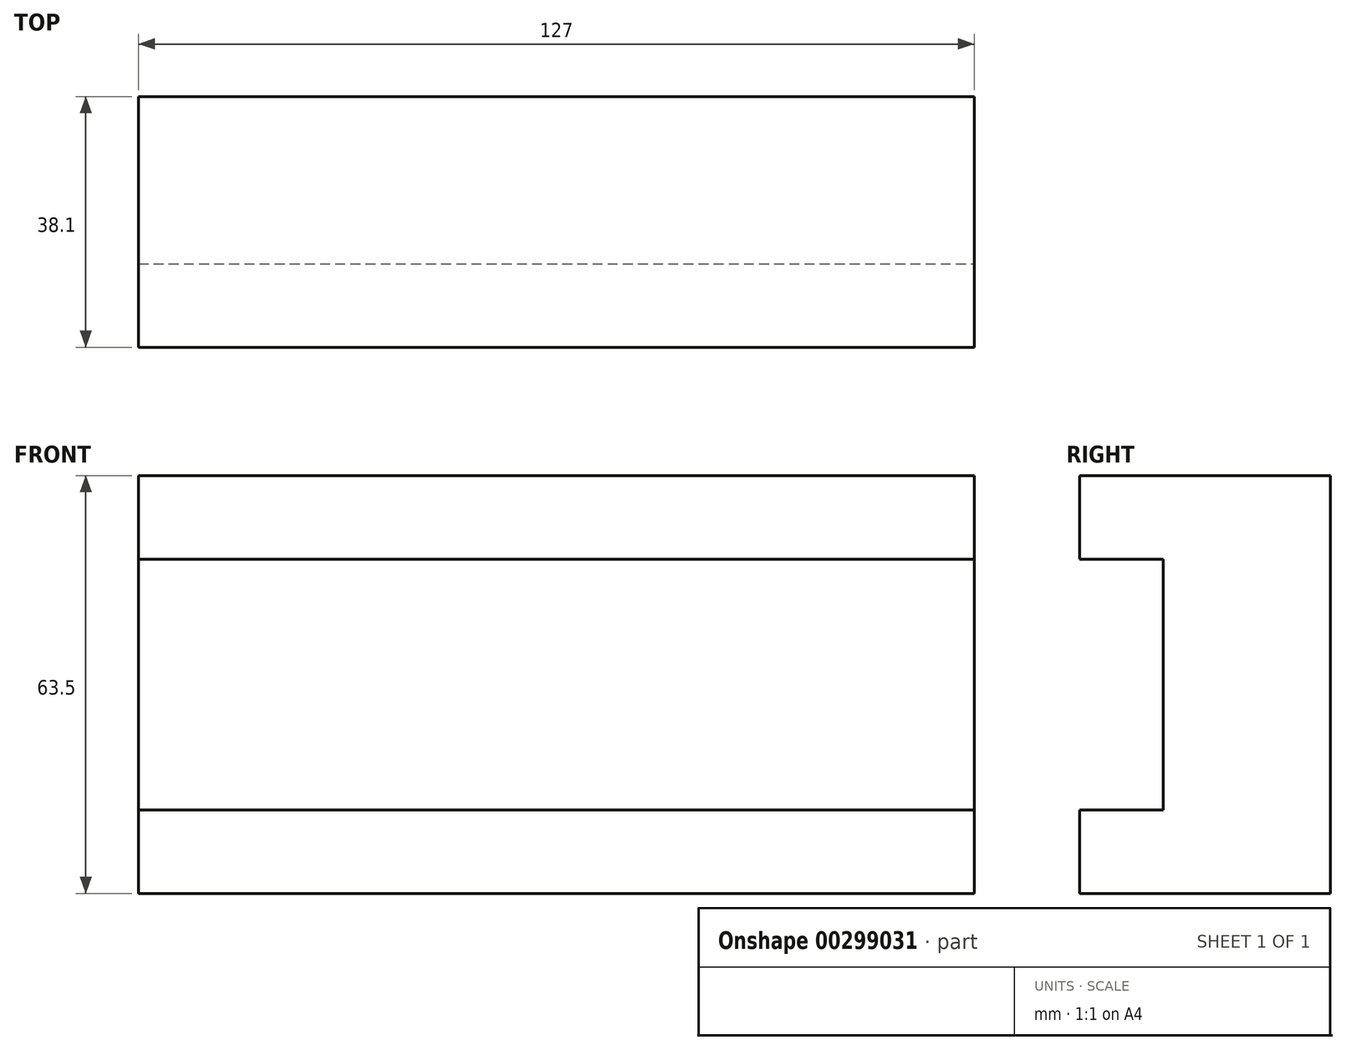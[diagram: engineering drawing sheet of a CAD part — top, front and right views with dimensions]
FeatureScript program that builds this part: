
annotation { "Feature Type Name" : "Feature", "Feature Type Description" : "" }
export const myFeature = defineFeature(function(context is Context, id is Id, definition is map)
    precondition{}
    {
        {
            var Q0;
            Q0=qCreatedBy(makeId("Front.planeOp"),FACE);
            var sketch = newSketch(context, id + "F0", { "sketchPlane" : qUnion([Q0])});
            skLineSegment(sketch, "E0.bottom", {"start": v(-63.5, 31.75) * mm, "end": v(63.5, 31.75) * mm});
            skLineSegment(sketch, "E0.top", {"start": v(-63.5, -31.75) * mm, "end": v(63.5, -31.75) * mm});
            skLineSegment(sketch, "E0.left", {"start": v(-63.5, 31.75) * mm, "end": v(-63.5, -31.75) * mm});
            skLineSegment(sketch, "E0.right", {"start": v(63.5, 31.75) * mm, "end": v(63.5, -31.75) * mm});
            skPoint(sketch, "E0.middle", {"position": v(0, 0) * mm});
            skSolve(sketch);
        }
        {
            var Q0;
            Q0=makeQuery(id+"F0.imprint","IMPRINT",FACE,{"disambiguationData":[TD([[makeQuery(id+"F0.imprint","IMPRINT",EDGE,{"derivedFrom":sQuery(id+"F0.wireOp",EDGE,"E0.bottom")}),-1.0]])]});
            extrude(context, id + "F1", {"entities" : qUnion([Q0]), "depth" : 38.1 * mm});
        }
        {
            var Q0;
            Q0=makeQuery(id+"F1.opExtrude","SWEPT_FACE",FACE,{"disambiguationData":[OSD([sQuery(id+"F0.wireOp",EDGE,"E0.right")])]});
            var sketch = newSketch(context, id + "F2", { "sketchPlane" : qUnion([Q0])});
            skLineSegment(sketch, "E1.bottom", {"start": v(-38.1, 19.05) * mm, "end": v(-25.4, 19.05) * mm});
            skLineSegment(sketch, "E1.top", {"start": v(-38.1, -19.05) * mm, "end": v(-25.4, -19.05) * mm});
            skLineSegment(sketch, "E1.left", {"start": v(-38.1, 19.05) * mm, "end": v(-38.1, -19.05) * mm});
            skLineSegment(sketch, "E1.right", {"start": v(-25.4, 19.05) * mm, "end": v(-25.4, -19.05) * mm});
            skSolve(sketch);
        }
        {
            var Q0;
            Q0=makeQuery(id+"F2.imprint","IMPRINT",FACE,{"disambiguationData":[TD([[makeQuery(id+"F2.imprint","IMPRINT",EDGE,{"derivedFrom":sQuery(id+"F2.wireOp",EDGE,"E1.bottom")}),-1.0]])]});
            extrude(context, id + "F3", {"entities" : qUnion([Q0]), "operationType" : NewBodyOperationType.REMOVE, "endBound" : BoundingType.THROUGH_ALL, "oppositeDirection" : true, "depth" : 25.4 * mm});
        }
    });
